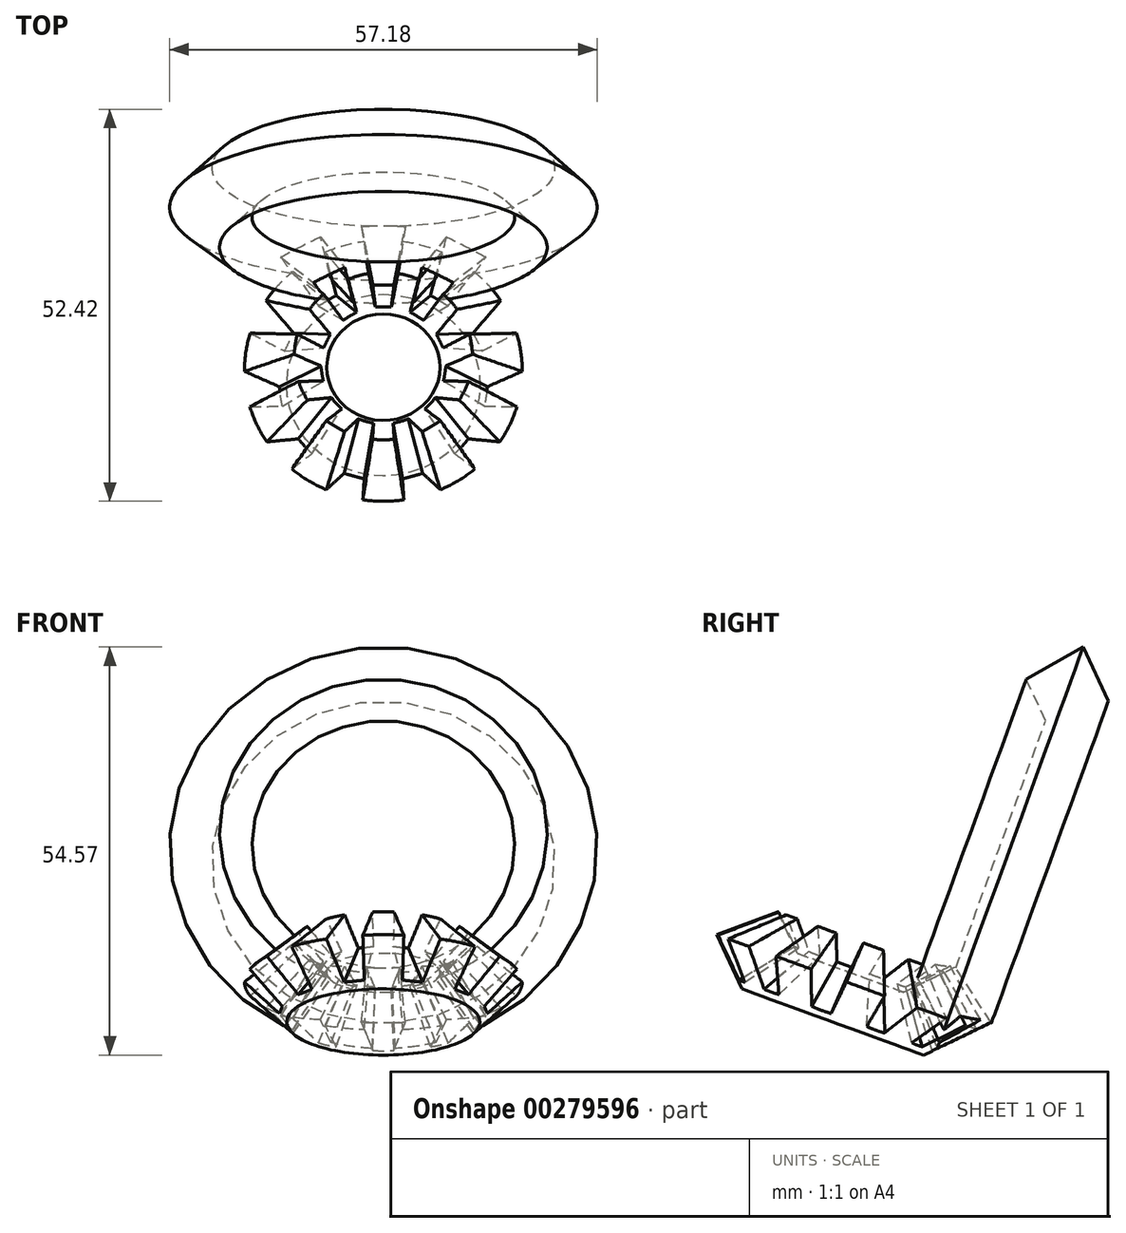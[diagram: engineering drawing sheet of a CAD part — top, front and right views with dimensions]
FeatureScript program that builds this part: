
annotation { "Feature Type Name" : "Feature", "Feature Type Description" : "" }
export const myFeature = defineFeature(function(context is Context, id is Id, definition is map)
    precondition{}
    {
        {
            var Q0;
            Q0=qCreatedBy(makeId("Right.planeOp"),FACE);
            var sketch = newSketch(context, id + "F0", { "sketchPlane" : qUnion([Q0])});
            skLineSegment(sketch, "E0", {"start": v(0, 0) * mm, "end": v(-18.8, 6.84) * mm});
            skLineSegment(sketch, "E1", {"start": v(0, 0) * mm, "end": v(10.26, 28.2) * mm});
            skLineSegment(sketch, "E2", {"start": v(0, 0) * mm, "end": v(-17.93, 38.45) * mm});
            skLineSegment(sketch, "E3", {"start": v(-6.64, 2.42) * mm, "end": v(2.42, 6.64) * mm});
            skLineSegment(sketch, "E4", {"start": v(-17.93, 38.45) * mm, "end": v(-6.64, 2.42) * mm});
            skLineSegment(sketch, "E5", {"start": v(-17.93, 38.45) * mm, "end": v(2.42, 6.64) * mm});
            skLineSegment(sketch, "E6", {"start": v(-17.93, 38.45) * mm, "end": v(-4.83, 3.26) * mm});
            skLineSegment(sketch, "E7.MirrorCS", {"start": v(-17.93, 38.45) * mm, "end": v(0.6, 5.8) * mm});
            skLineSegment(sketch, "E8", {"start": v(-17.93, 38.45) * mm, "end": v(20.52, 56.38) * mm});
            skSolve(sketch);
        }
        {
            var Q0;
            Q0=qCreatedBy(makeId("Right.planeOp"),FACE);
            var sketch = newSketch(context, id + "F1", { "sketchPlane" : qUnion([Q0])});
            skLineSegment(sketch, "E9", {"start": v(-4.83, 3.26) * mm, "end": v(2.42, 6.64) * mm});
            skLineSegment(sketch, "E10", {"start": v(2.42, 6.64) * mm, "end": v(10.26, 28.2) * mm});
            skLineSegment(sketch, "E11", {"start": v(10.26, 28.2) * mm, "end": v(3.68, 30.58) * mm});
            skLineSegment(sketch, "E12", {"start": v(3.68, 30.58) * mm, "end": v(-2.33, 14.07) * mm});
            skLineSegment(sketch, "E13", {"start": v(-2.33, 14.07) * mm, "end": v(-7.89, 11.47) * mm});
            skLineSegment(sketch, "E14", {"start": v(-7.89, 11.47) * mm, "end": v(-4.83, 3.26) * mm});
            skSolve(sketch);
        }
        {
            var Q0;
            Q0=makeQuery(id+"F1.imprint","IMPRINT",FACE,{"disambiguationData":[TD([[makeQuery(id+"F1.imprint","IMPRINT",EDGE,{"derivedFrom":sQuery(id+"F1.wireOp",EDGE,"E9")}),1.0]])]});
            var Q1;
            Q1=sQuery(id+"F1.wireOp",EDGE,"E11");
            revolve(context, id + "F2", {"entities" : qUnion([Q0]), "axis" : qUnion([Q1]), "revolveType" : RevolveType.FULL});
        }
        {
            var Q0;
            Q0=qCreatedBy(makeId("Right.planeOp"),FACE);
            var sketch = newSketch(context, id + "F3", { "sketchPlane" : qUnion([Q0])});
            skLineSegment(sketch, "E15", {"start": v(0.6, 5.8) * mm, "end": v(-3.72, 13.42) * mm});
            skLineSegment(sketch, "E16", {"start": v(0.6, 5.8) * mm, "end": v(-6.64, 2.42) * mm});
            skLineSegment(sketch, "E17", {"start": v(-6.64, 2.42) * mm, "end": v(-18.8, 6.84) * mm});
            skLineSegment(sketch, "E18", {"start": v(-18.8, 6.84) * mm, "end": v(-16.4, 13.42) * mm});
            skLineSegment(sketch, "E19", {"start": v(-16.4, 13.42) * mm, "end": v(-9.28, 10.83) * mm});
            skLineSegment(sketch, "E20", {"start": v(-9.28, 10.83) * mm, "end": v(-3.72, 13.42) * mm});
            skSolve(sketch);
        }
        {
            var Q0;
            Q0 = qSketchRegion(id + "F3", true);
            var Q1;
            Q1=sQuery(id+"F3.wireOp",EDGE,"E18");
            revolve(context, id + "F4", {"entities" : qUnion([Q0]), "axis" : qUnion([Q1]), "revolveType" : RevolveType.FULL});
        }
        {
            var Q0;
            Q0=sQuery(id+"F0.wireOp",EDGE,"E2");
            var Q1;
            Q1=sQuery(id+"F0.wireOp",VERTEX,"E2.start");
            cPlane(context, id + "F5", {"entities" : qUnion([Q0, Q1]), "cplaneType" : CPlaneType.LINE_POINT, "offset" : 25 * mm, "width" : 150 * mm, "height" : 150 * mm});
        }
        {
            var Q0;
            Q0=qCreatedBy(makeId("Right.planeOp"),FACE);
            var sketch = newSketch(context, id + "F6", { "sketchPlane" : qUnion([Q0])});
            skLineSegment(sketch, "E21", {"start": v(0, 0) * mm, "end": v(38.45, 17.93) * mm});
            skLineSegment(sketch, "E22", {"start": v(38.45, 17.93) * mm, "end": v(20.52, 56.38) * mm});
            skLineSegment(sketch, "E23", {"start": v(0, 0) * mm, "end": v(-38.45, -17.93) * mm});
            skSolve(sketch);
        }
        {
            var Q0;
            Q0=qCreatedBy(id+"F5.planeOp",FACE);
            var sketch = newSketch(context, id + "F7", { "sketchPlane" : qUnion([Q0])});
            skLineSegment(sketch, "E24", {"start": v(0, -13.14) * mm, "end": v(3.32, 5.71) * mm});
            skLineSegment(sketch, "E25", {"start": v(3.32, 5.71) * mm, "end": v(0, 5.71) * mm});
            skLineSegment(sketch, "E26.MirrorCS", {"start": v(-3.32, 5.71) * mm, "end": v(0, 5.71) * mm});
            skLineSegment(sketch, "E27.MirrorCS", {"start": v(0, -13.14) * mm, "end": v(-3.32, 5.71) * mm});
            skLineSegment(sketch, "E28", {"start": v(1.59, -4.14) * mm, "end": v(-1.59, -4.14) * mm});
            skSolve(sketch);
        }
        {
            var Q0;
            {var subQ3=sQuery(id+"F7.wireOp",EDGE,"E25");Q0=makeQuery(id+"F7.imprint","IMPRINT",FACE,{"disambiguationData":[TD([[makeQuery(id+"F7.imprint","IMPRINT",EDGE,{"derivedFrom":subQ3}),1.0]])]});}
            var Q1;
            Q1=sQuery(id+"F0.wireOp",VERTEX,"E6.start");
            loft(context, id + "F8", {"sheetProfilesArray" : [{ "sheetProfileEntities" : qUnion([Q0]) }, { "sheetProfileEntities" : qUnion([Q1]) }]});
        }
        {
            var Q0;
            {var subQ3=sQuery(id+"F7.wireOp",EDGE,"E25");Q0=makeQuery(id+"F8.opLoft","SWEPT_BODY",BODY,{"disambiguationData":[OSD([sQuery(id+"F0.wireOp",VERTEX,"E6.start"),makeQuery(id+"F7.imprint","IMPRINT",FACE,{"disambiguationData":[TD([[makeQuery(id+"F7.imprint","IMPRINT",EDGE,{"derivedFrom":subQ3}),1.0]])]})])]});}
            var Q1;
            Q1=makeQuery(id+"F4.opRevolve","SWEPT_EDGE",EDGE,{"disambiguationData":[OSD([sQuery(id+"F3.wireOp",EDGE,"E16"),sQuery(id+"F3.wireOp",EDGE,"E17")])]});
            circularPattern(context, id + "F9", {"operationType" : NewBodyOperationType.REMOVE, "entities" : qUnion([Q0]), "axis" : qUnion([Q1]), "angle" : 360 * degree, "instanceCount" : 11, "equalSpace" : true});
        }
    });
